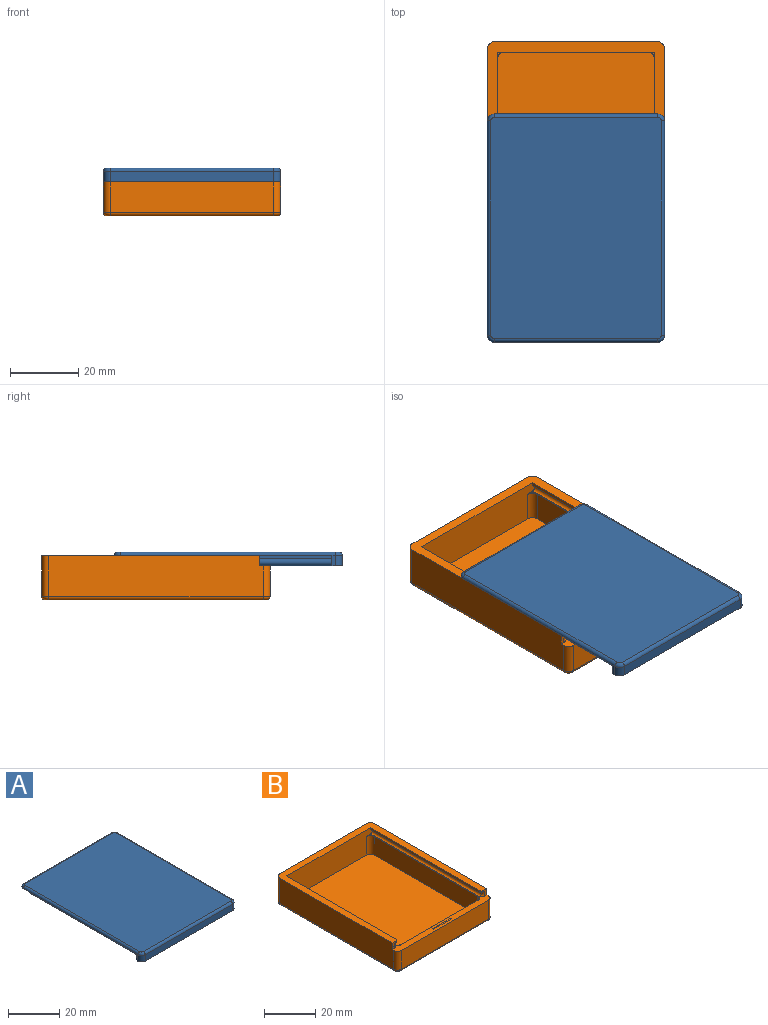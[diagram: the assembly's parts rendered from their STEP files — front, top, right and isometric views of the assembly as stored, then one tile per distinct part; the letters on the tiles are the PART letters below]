
ASSEMBLY  parts=2 mates=1
PART A: 36 faces, bbox 52.3x67.3x4 mm
  f0: plane 63x52mm, normal (0,0,-1), area 602.3mm2, adj f1,f2,f3,f4,f6,f7,f9,f11
  f1: cylinder r=1mm len=60mm, axis (0,-1,0), area 188.5mm2, adj f0,f12,f13,f22
  f2: plane 3x1mm, normal (-1,0,0), area 3mm2, adj f0,f6,f11,f30
  f3: plane 3x1mm, normal (1,0,0), area 3mm2, adj f0,f7,f13,f27
  f4: plane 48x3mm, normal (0,-1,0), area 144mm2, adj f0,f6,f7,f31
  f5: plane 65x50mm, normal (0,0,1), area 3249.1mm2, adj f25,f26,f27,f28,f29,f30,f31,f32
  f6: cylinder r=2mm len=3mm, axis (0,0,-1), area 9.4mm2, adj f0,f2,f4,f32
  f7: cylinder r=2mm len=3mm, axis (0,0,1), area 9.4mm2, adj f0,f3,f4,f29
  f8: plane 64x52mm, normal (0,0,-1), area 532.9mm2, adj f10,f11,f12,f13,f16,f19,f23,f25
  f9: cylinder r=1mm len=60mm, axis (0,-1,0), area 188.5mm2, adj f0,f10,f11,f20
  f10: plane 60x1mm, normal (-1,0,0), area 60mm2, adj f8,f9,f11,f19
  f11: plane 3.1x3mm, normal (0,1,0), area 7.7mm2, adj f0,f2,f8,f9,f10
  f12: plane 60x1mm, normal (1,0,0), area 60mm2, adj f1,f8,f13,f23
  f13: plane 3.1x3mm, normal (0,1,0), area 7.7mm2, adj f0,f1,f3,f8,f12
  f14: plane 57x41mm, normal (0,0,-1), area 2337mm2, adj f15,f16,f17,f18
  f15: plane 57x2mm, normal (-1,0,0), area 113.8mm2, adj f0,f14,f16,f18,f24
  f16: plane 43.8x2mm, normal (0,1,0), area 46.6mm2, adj f8,f14,f15,f17,f19,f21,f23,f24
  f17: plane 57x2mm, normal (1,0,0), area 113.8mm2, adj f0,f14,f16,f18,f21
  f18: plane 41x2mm, normal (0,1,0), area 82mm2, adj f0,f14,f15,f17
  f19: cylinder r=1mm len=3mm, axis (0,0,1), area 5.8mm2, adj f8,f10,f16,f20,f21
  f20: sphere r=1mm, area 8.6mm2, adj f9,f19
  f21: cylinder r=1mm len=2.4mm, axis (1,0,0), area 3.2mm2, adj f0,f16,f17,f19
  f22: sphere r=1mm, area 8.6mm2, adj f1,f23
  f23: cylinder r=1mm len=3mm, axis (0,0,-1), area 5.8mm2, adj f8,f12,f16,f22,f24
  f24: cylinder r=1mm len=2.4mm, axis (-1,0,0), area 3.2mm2, adj f0,f15,f16,f23
  f25: torus R=1mm, axis (0,0,1), area 4mm2, adj f5,f8,f26,f27
  f26: cylinder r=1mm len=48mm, axis (1,0,0), area 75.4mm2, adj f5,f8,f25,f28
  f27: cylinder r=1mm len=63mm, axis (0,-1,0), area 99mm2, adj f3,f5,f8,f25,f29
  f28: torus R=1mm, axis (0,0,1), area 4mm2, adj f5,f8,f26,f30
  f29: torus R=1mm, axis (0,0,1), area 4mm2, adj f5,f7,f27,f31
  f30: cylinder r=1mm len=63mm, axis (0,1,0), area 99mm2, adj f2,f5,f8,f28,f32
  f31: cylinder r=1mm len=48mm, axis (-1,0,0), area 75.4mm2, adj f4,f5,f29,f32
  f32: torus R=1mm, axis (0,0,1), area 4mm2, adj f5,f6,f30,f31
  f33: sphere r=0.2mm, area 0.1mm2, adj f0,f34
  f34: cylinder r=0.2mm len=9.6mm, axis (-1,0,0), area 6mm2, adj f0,f33,f35
  f35: sphere r=0.2mm, area 0.1mm2, adj f0,f34
PART B: 54 faces, bbox 52.4x67.4x14 mm
  f0: plane 63x12mm, normal (1,0,0), area 753mm2, adj f4,f5,f19,f23,f24,f30
  f1: plane 63x12mm, normal (-1,0,0), area 753mm2, adj f4,f6,f20,f23,f25,f33
  f2: plane 60x1mm, normal (1,0,0), area 60mm2, adj f4,f7,f12,f37
  f3: plane 60x1mm, normal (-1,0,0), area 60mm2, adj f4,f8,f12,f39
  f4: plane 64x52mm, normal (0,0,1), area 519.9mm2, adj f0,f1,f2,f3,f10,f12,f19,f20
  f5: cylinder r=2mm len=9mm, axis (0,0,1), area 28.3mm2, adj f0,f9,f23,f28
  f6: cylinder r=2mm len=9mm, axis (0,0,-1), area 28.3mm2, adj f1,f9,f23,f31
  f7: cylinder r=1mm len=60mm, axis (0,-1,0), area 178.7mm2, adj f2,f12,f21,f23,f36,f41,f42,f43
  f8: cylinder r=1mm len=60mm, axis (0,-1,0), area 178.7mm2, adj f3,f12,f22,f23,f38,f47,f48,f49
  f9: plane 48x9mm, normal (0,-1,0), area 432mm2, adj f5,f6,f23,f29
  f10: plane 48x12mm, normal (0,1,0), area 576mm2, adj f4,f19,f20,f34
  f11: plane 57x8.82mm, normal (1,0,0), area 502.6mm2, adj f15,f18,f27,f42
  f12: plane 48.04x12.04mm, normal (0,-1,0), area 519.3mm2, adj f2,f3,f4,f7,f8,f15,f16,f21
  f13: plane 57x8.82mm, normal (-1,0,0), area 502.6mm2, adj f16,f17,f27,f48
  f14: plane 42x8.8mm, normal (0,1,0), area 369.6mm2, adj f17,f18,f27,f45
  f15: cylinder r=2mm len=8.82mm, axis (0,0,-1), area 27.7mm2, adj f11,f12,f27,f40,f41
  f16: cylinder r=2mm len=8.82mm, axis (0,0,1), area 27.7mm2, adj f12,f13,f27,f49,f50
  f17: cylinder r=2mm len=8.82mm, axis (0,0,-1), area 27.7mm2, adj f13,f14,f27,f46,f47
  f18: cylinder r=2mm len=8.82mm, axis (0,0,1), area 27.7mm2, adj f11,f14,f27,f43,f44
  f19: cylinder r=2mm len=12mm, axis (0,0,-1), area 37.7mm2, adj f0,f4,f10,f32
  f20: cylinder r=2mm len=12mm, axis (0,0,1), area 37.7mm2, adj f1,f4,f10,f35
  f21: plane 1.08x1.08mm, normal (0,0,1), area 0.4mm2, adj f7,f12,f40
  f22: plane 1.08x1.08mm, normal (0,0,1), area 0.4mm2, adj f8,f12,f50
  f23: plane 52x4.08mm, normal (0,0,1), area 143.8mm2, adj f0,f1,f5,f6,f7,f8,f9,f24
  f24: plane 3x2mm, normal (0,-1,0), area 3.9mm2, adj f0,f4,f23,f38,f39
  f25: plane 3x2mm, normal (0,-1,0), area 3.9mm2, adj f1,f4,f23,f36,f37
  f26: plane 65x50mm, normal (0,0,-1), area 3249.1mm2, adj f28,f29,f30,f31,f32,f33,f34,f35
  f27: plane 61x46mm, normal (0,0,1), area 2802.6mm2, adj f11,f12,f13,f14,f15,f16,f17,f18
  f28: torus R=1mm, axis (0,0,1), area 4mm2, adj f5,f26,f29,f30
  f29: cylinder r=1mm len=48mm, axis (1,0,0), area 75.4mm2, adj f9,f26,f28,f31
  f30: cylinder r=1mm len=63mm, axis (0,1,0), area 99mm2, adj f0,f26,f28,f32
  f31: torus R=1mm, axis (0,0,1), area 4mm2, adj f6,f26,f29,f33
  f32: torus R=1mm, axis (0,0,1), area 4mm2, adj f19,f26,f30,f34
  f33: cylinder r=1mm len=63mm, axis (0,-1,0), area 99mm2, adj f1,f26,f31,f35
  f34: cylinder r=1mm len=48mm, axis (-1,0,0), area 75.4mm2, adj f10,f26,f32,f35
  f35: torus R=1mm, axis (0,0,1), area 4mm2, adj f20,f26,f33,f34
  f36: torus R=2mm, axis (0,-1,0), area 4.7mm2, adj f7,f23,f25,f37
  f37: cylinder r=1mm len=1mm, axis (0,0,-1), area 1.1mm2, adj f2,f4,f25,f36
  f38: torus R=2mm, axis (0,-1,0), area 4.7mm2, adj f8,f23,f24,f39
  f39: cylinder r=1mm len=1mm, axis (0,0,1), area 1.1mm2, adj f3,f4,f24,f38
  f40: torus R=2.2mm, axis (0,0,-1), area 0.6mm2, adj f12,f15,f21,f41
  f41: bspline ~1.49x0.41mm, area 0.3mm2, adj f7,f15,f40,f42
  f42: cylinder r=0.2mm len=57mm, axis (0,-1,0), area 16mm2, adj f7,f11,f41,f43
  f43: bspline ~1.31x0.47mm, area 0.3mm2, adj f7,f18,f42,f44
  f44: torus R=2.2mm, axis (0,0,-1), area 0.7mm2, adj f18,f23,f43,f45
  f45: cylinder r=0.2mm len=42mm, axis (1,0,0), area 13.2mm2, adj f14,f23,f44,f46
  f46: torus R=2.2mm, axis (0,0,-1), area 0.7mm2, adj f17,f23,f45,f47
  f47: bspline ~1.31x0.47mm, area 0.3mm2, adj f8,f17,f46,f48
  f48: cylinder r=0.2mm len=57mm, axis (0,-1,0), area 16mm2, adj f8,f13,f47,f49
  f49: bspline ~1.49x0.41mm, area 0.3mm2, adj f8,f16,f48,f50
  f50: torus R=2.2mm, axis (0,0,-1), area 0.6mm2, adj f12,f16,f22,f49
  f51: sphere r=0.2mm, area 0.1mm2, adj f23,f52
  f52: cylinder r=0.2mm len=9.6mm, axis (1,0,0), area 6mm2, adj f23,f51,f53
  f53: sphere r=0.2mm, area 0.1mm2, adj f23,f52
PLACE A t=(-27.18,45.37,-46.18)mm
PLACE B t=(60.99,66.56,-55.25)mm
MATE slider B.f25 <-> A.f11  axis (0,-1,0) through (-12.03,36.06,-44.58)mm
